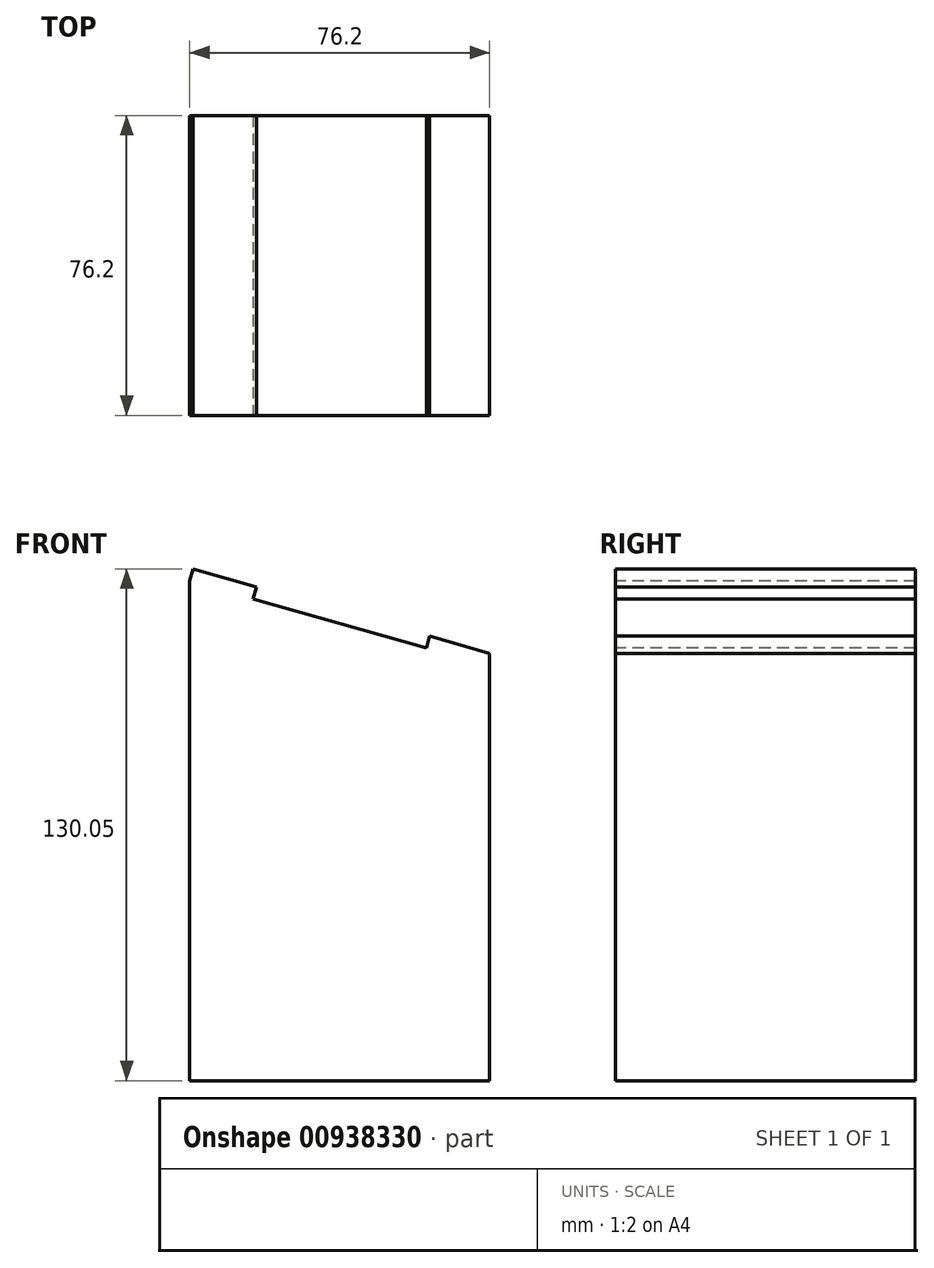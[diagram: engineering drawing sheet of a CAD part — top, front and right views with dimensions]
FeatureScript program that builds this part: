
annotation { "Feature Type Name" : "Feature", "Feature Type Description" : "" }
export const myFeature = defineFeature(function(context is Context, id is Id, definition is map)
    precondition{}
    {
        {
            var Q0;
            Q0=qCreatedBy(makeId("Top.planeOp"),FACE);
            var sketch = newSketch(context, id + "F0", { "sketchPlane" : qUnion([Q0])});
            skLineSegment(sketch, "E0.bottom", {"start": v(37.96, 48.2) * mm, "end": v(-38.24, 48.2) * mm});
            skLineSegment(sketch, "E0.top", {"start": v(37.96, -28) * mm, "end": v(-38.24, -28) * mm});
            skLineSegment(sketch, "E0.left", {"start": v(37.96, 48.2) * mm, "end": v(37.96, -28) * mm});
            skLineSegment(sketch, "E0.right", {"start": v(-38.24, 48.2) * mm, "end": v(-38.24, -28) * mm});
            skPoint(sketch, "E0.middle", {"position": v(-0.14, 10.1) * mm});
            skSolve(sketch);
        }
        {
            var Q0;
            Q0=makeQuery(id+"F0.imprint","IMPRINT",FACE,{"disambiguationData":[TD([[makeQuery(id+"F0.imprint","IMPRINT",EDGE,{"derivedFrom":sQuery(id+"F0.wireOp",EDGE,"E0.bottom")}),1.0]])]});
            extrude(context, id + "F1", {"entities" : qUnion([Q0]), "depth" : 127 * mm, "offsetDistance" : 25.4 * mm});
        }
        {
            var Q0;
            Q0=makeQuery(id+"F1.opExtrude","SWEPT_FACE",FACE,{"disambiguationData":[OSD([sQuery(id+"F0.wireOp",EDGE,"E0.top")])]});
            var sketch = newSketch(context, id + "F2", { "sketchPlane" : qUnion([Q0])});
            skLineSegment(sketch, "E1", {"start": v(-38.24, 127) * mm, "end": v(37.96, 127) * mm});
            skLineSegment(sketch, "E2", {"start": v(37.96, 127) * mm, "end": v(37.96, 105.29) * mm});
            skLineSegment(sketch, "E3", {"start": v(37.96, 105.29) * mm, "end": v(-38.24, 127) * mm});
            skSolve(sketch);
        }
        {
            var Q0;
            Q0=makeQuery(id+"F2.imprint","IMPRINT",FACE,{"disambiguationData":[TD([[makeQuery(id+"F2.imprint","IMPRINT",EDGE,{"derivedFrom":sQuery(id+"F2.wireOp",EDGE,"E1")}),1.0]])]});
            extrude(context, id + "F3", {"entities" : qUnion([Q0]), "operationType" : NewBodyOperationType.REMOVE, "endBound" : BoundingType.THROUGH_ALL, "oppositeDirection" : true, "depth" : 25.4 * mm, "offsetDistance" : 25.4 * mm});
        }
        {
            var Q0;
            Q0=makeQuery(id+"F3.boolean.opBoolean","COPY",FACE,{"derivedFrom":makeQuery(id+"F3.opExtrude","SWEPT_FACE",FACE,{"disambiguationData":[OSD([sQuery(id+"F2.wireOp",EDGE,"E3")])]})});
            var sketch = newSketch(context, id + "F4", { "sketchPlane" : qUnion([Q0])});
            skLineSegment(sketch, "E4.bottom", {"start": v(-71.58, 48.2) * mm, "end": v(-54.82, 48.2) * mm});
            skLineSegment(sketch, "E4.top", {"start": v(-71.58, -28) * mm, "end": v(-54.82, -28) * mm});
            skLineSegment(sketch, "E4.left", {"start": v(-71.58, 48.2) * mm, "end": v(-71.58, -28) * mm});
            skLineSegment(sketch, "E4.right", {"start": v(-54.82, 48.2) * mm, "end": v(-54.82, -28) * mm});
            skLineSegment(sketch, "E5.bottom", {"start": v(7.65, 48.2) * mm, "end": v(-9.11, 48.2) * mm});
            skLineSegment(sketch, "E5.top", {"start": v(7.65, -28) * mm, "end": v(-9.11, -28) * mm});
            skLineSegment(sketch, "E5.left", {"start": v(7.65, 48.2) * mm, "end": v(7.65, -28) * mm});
            skLineSegment(sketch, "E5.right", {"start": v(-9.11, 48.2) * mm, "end": v(-9.11, -28) * mm});
            skSolve(sketch);
        }
        {
            var Q0;
            Q0=makeQuery(id+"F4.imprint","IMPRINT",FACE,{"disambiguationData":[TD([[makeQuery(id+"F4.imprint","IMPRINT",EDGE,{"derivedFrom":sQuery(id+"F4.wireOp",EDGE,"E4.bottom")}),1.0]])]});
            var Q1;
            Q1=makeQuery(id+"F4.imprint","IMPRINT",FACE,{"disambiguationData":[TD([[makeQuery(id+"F4.imprint","IMPRINT",EDGE,{"derivedFrom":sQuery(id+"F4.wireOp",EDGE,"E5.bottom")}),1.0]])]});
            extrude(context, id + "F5", {"entities" : qUnion([Q0, Q1]), "operationType" : NewBodyOperationType.ADD, "depth" : 3.17 * mm, "offsetDistance" : 25.4 * mm});
        }
        {
            var Q0;
            Q0=makeQuery(id+"F5.boolean.opBoolean","MERGE",FACE,{"derivedFrom":[makeQuery(id+"F1.opExtrude","SWEPT_FACE",FACE,{"disambiguationData":[OSD([sQuery(id+"F0.wireOp",EDGE,"E0.top")])]}),makeQuery(id+"F5.opExtrude","SWEPT_FACE",FACE,{"disambiguationData":[OSD([sQuery(id+"F4.wireOp",EDGE,"E4.top")])]}),makeQuery(id+"F5.opExtrude","SWEPT_FACE",FACE,{"disambiguationData":[OSD([sQuery(id+"F4.wireOp",EDGE,"E5.top")])]})]});
            var sketch = newSketch(context, id + "F6", { "sketchPlane" : qUnion([Q0])});
            skLineSegment(sketch, "E6", {"start": v(37.96, 105.29) * mm, "end": v(37.96, 108.6) * mm});
            skSolve(sketch);
        }
        {
            var Q0;
            {var subQ0=sQuery(id+"F6.wireOp",EDGE,"E6");Q0=makeQuery(id+"F6.imprint","IMPRINT",FACE,{"disambiguationData":[TD([[makeQuery(id+"F6.imprint","IMPRINT",EDGE,{"derivedFrom":subQ0}),-1.0]])]});}
            extrude(context, id + "F7", {"entities" : qUnion([Q0]), "operationType" : NewBodyOperationType.REMOVE, "endBound" : BoundingType.THROUGH_ALL, "oppositeDirection" : true, "depth" : 25.4 * mm, "offsetDistance" : 25.4 * mm});
        }
    });
